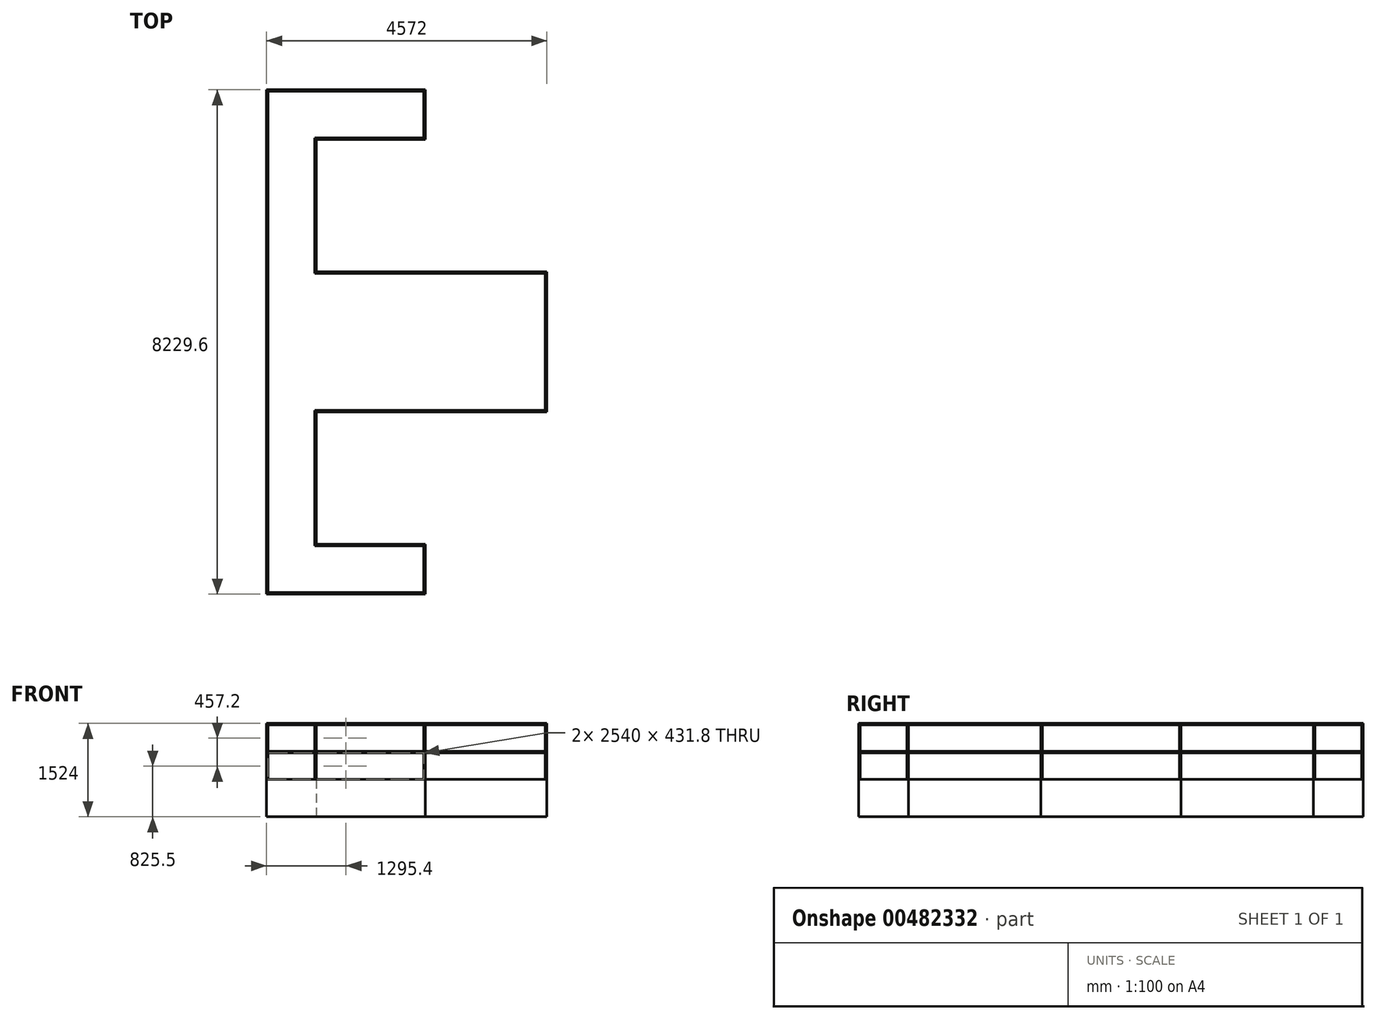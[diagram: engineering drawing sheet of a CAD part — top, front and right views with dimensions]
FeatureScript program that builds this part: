
annotation { "Feature Type Name" : "Feature", "Feature Type Description" : "" }
export const myFeature = defineFeature(function(context is Context, id is Id, definition is map)
    precondition{}
    {
        {
            var Q0;
            Q0=qCreatedBy(makeId("Top.planeOp"),FACE);
            var sketch = newSketch(context, id + "F0", { "sketchPlane" : qUnion([Q0])});
            skLineSegment(sketch, "E0", {"start": v(0, 0) * mm, "end": v(3759.2, 0) * mm});
            skLineSegment(sketch, "E1", {"start": v(3759.2, 0) * mm, "end": v(3759.2, 2286) * mm});
            skLineSegment(sketch, "E2", {"start": v(3759.2, 2286) * mm, "end": v(0, 2286) * mm});
            skLineSegment(sketch, "E3", {"start": v(0, 2286) * mm, "end": v(0, 4445) * mm});
            skLineSegment(sketch, "E4", {"start": v(0, 4445) * mm, "end": v(1778, 4445) * mm});
            skLineSegment(sketch, "E5", {"start": v(1778, 5257.8) * mm, "end": v(-812.8, 5257.8) * mm});
            skLineSegment(sketch, "E6", {"start": v(-812.8, 5257.8) * mm, "end": v(-812.8, -2971.8) * mm});
            skLineSegment(sketch, "E7", {"start": v(-812.8, -2971.8) * mm, "end": v(1778, -2971.8) * mm});
            skLineSegment(sketch, "E8", {"start": v(1778, -2971.8) * mm, "end": v(1778, -2159) * mm});
            skLineSegment(sketch, "E9", {"start": v(1778, -2159) * mm, "end": v(0, -2159) * mm});
            skLineSegment(sketch, "E10", {"start": v(0, -2159) * mm, "end": v(0, 0) * mm});
            skLineSegment(sketch, "E11", {"start": v(1778, 5257.8) * mm, "end": v(1778, 4445) * mm});
            skSolve(sketch);
        }
        {
            var Q0;
            Q0 = qSketchRegion(id + "F0", true);
            extrude(context, id + "F1", {"entities" : qUnion([Q0]), "depth" : 609.6 * mm, "offsetDistance" : 25.4 * mm});
        }
        {
            var Q0;
            Q0=makeQuery(id+"F1.opExtrude","CAP_FACE",FACE,{"disambiguationData":[OSD([sQuery(id+"F0.wireOp",EDGE,"E0"),sQuery(id+"F0.wireOp",EDGE,"E1"),sQuery(id+"F0.wireOp",EDGE,"E2"),sQuery(id+"F0.wireOp",EDGE,"E3"),sQuery(id+"F0.wireOp",EDGE,"E4"),sQuery(id+"F0.wireOp",EDGE,"E5"),sQuery(id+"F0.wireOp",EDGE,"E6"),sQuery(id+"F0.wireOp",EDGE,"E7"),sQuery(id+"F0.wireOp",EDGE,"E8"),sQuery(id+"F0.wireOp",EDGE,"E9"),sQuery(id+"F0.wireOp",EDGE,"E10"),sQuery(id+"F0.wireOp",EDGE,"E11")])],"isStart":false});
            var sketch = newSketch(context, id + "F2", { "sketchPlane" : qUnion([Q0])});
            skLineSegment(sketch, "E12.0", {"start": v(-787.4, -2946.4) * mm, "end": v(1752.6, -2946.4) * mm});
            skLineSegment(sketch, "E12.1", {"start": v(3733.8, 25.4) * mm, "end": v(3733.8, 2260.6) * mm});
            skLineSegment(sketch, "E12.2", {"start": v(-25.4, 25.4) * mm, "end": v(3733.8, 25.4) * mm});
            skLineSegment(sketch, "E12.3", {"start": v(-25.4, -2184.4) * mm, "end": v(-25.4, 25.4) * mm});
            skLineSegment(sketch, "E12.4", {"start": v(1752.6, -2184.4) * mm, "end": v(-25.4, -2184.4) * mm});
            skLineSegment(sketch, "E12.5", {"start": v(3733.8, 2260.6) * mm, "end": v(-25.4, 2260.6) * mm});
            skLineSegment(sketch, "E12.6", {"start": v(1752.6, -2946.4) * mm, "end": v(1752.6, -2184.4) * mm});
            skLineSegment(sketch, "E12.7", {"start": v(-25.4, 2260.6) * mm, "end": v(-25.4, 4470.4) * mm});
            skLineSegment(sketch, "E12.8", {"start": v(-25.4, 4470.4) * mm, "end": v(1752.6, 4470.4) * mm});
            skLineSegment(sketch, "E12.9", {"start": v(1752.6, 4470.4) * mm, "end": v(1752.6, 5232.4) * mm});
            skLineSegment(sketch, "E12.10", {"start": v(1752.6, 5232.4) * mm, "end": v(-787.4, 5232.4) * mm});
            skLineSegment(sketch, "E12.11", {"start": v(-787.4, 5232.4) * mm, "end": v(-787.4, -2946.4) * mm});
            skSolve(sketch);
        }
        {
            var Q0;
            Q0=makeQuery(id+"F2.imprint","IMPRINT",FACE,{"disambiguationData":[TD([[makeQuery(id+"F2.imprint","IMPRINT",EDGE,{"derivedFrom":sQuery(id+"F2.wireOp",EDGE,"E12.0")}),-1.0]])]});
            extrude(context, id + "F3", {"entities" : qUnion([Q0]), "operationType" : NewBodyOperationType.ADD, "depth" : 914.4 * mm, "offsetDistance" : 25.4 * mm});
        }
        {
            var Q0;
            {var subQ0=sQuery(id+"F0.wireOp",EDGE,"E6");Q0=makeQuery(id+"F3.boolean.opBoolean","MERGE",FACE,{"derivedFrom":[makeQuery(id+"F1.opExtrude","SWEPT_FACE",FACE,{"disambiguationData":[OSD([subQ0])]}),makeQuery(id+"F3.opExtrude","SWEPT_FACE",FACE,{"disambiguationData":[OSD([subQ0])]})]});}
            var sketch = newSketch(context, id + "F4", { "sketchPlane" : qUnion([Q0])});
            skLineSegment(sketch, "E13.bottom", {"start": v(-5232.4, 1498.6) * mm, "end": v(2946.4, 1498.6) * mm});
            skLineSegment(sketch, "E13.top", {"start": v(-5232.4, 1066.8) * mm, "end": v(2946.4, 1066.8) * mm});
            skLineSegment(sketch, "E13.left", {"start": v(-5232.4, 1498.6) * mm, "end": v(-5232.4, 1066.8) * mm});
            skLineSegment(sketch, "E13.right", {"start": v(2946.4, 1498.6) * mm, "end": v(2946.4, 1066.8) * mm});
            skLineSegment(sketch, "E14.bottom", {"start": v(-5232.4, 1041.4) * mm, "end": v(2946.4, 1041.4) * mm});
            skLineSegment(sketch, "E14.top", {"start": v(-5232.4, 609.6) * mm, "end": v(2946.4, 609.6) * mm});
            skLineSegment(sketch, "E14.left", {"start": v(-5232.4, 1041.4) * mm, "end": v(-5232.4, 609.6) * mm});
            skLineSegment(sketch, "E14.right", {"start": v(2946.4, 1041.4) * mm, "end": v(2946.4, 609.6) * mm});
            skSolve(sketch);
        }
        {
            var Q0;
            Q0 = qSketchRegion(id + "F4", true);
            extrude(context, id + "F5", {"entities" : qUnion([Q0]), "operationType" : NewBodyOperationType.REMOVE, "oppositeDirection" : true, "depth" : 50.8 * mm, "offsetDistance" : 25.4 * mm});
        }
        {
            var Q0;
            {var subQ0=sQuery(id+"F0.wireOp",EDGE,"E7");Q0=makeQuery(id+"F3.boolean.opBoolean","MERGE",FACE,{"derivedFrom":[makeQuery(id+"F1.opExtrude","SWEPT_FACE",FACE,{"disambiguationData":[OSD([subQ0])]}),makeQuery(id+"F3.opExtrude","SWEPT_FACE",FACE,{"disambiguationData":[OSD([subQ0])]})]});}
            var sketch = newSketch(context, id + "F6", { "sketchPlane" : qUnion([Q0])});
            skLineSegment(sketch, "E15.bottom", {"start": v(-787.4, 1498.6) * mm, "end": v(1752.6, 1498.6) * mm});
            skLineSegment(sketch, "E15.top", {"start": v(-787.4, 1066.8) * mm, "end": v(1752.6, 1066.8) * mm});
            skLineSegment(sketch, "E15.left", {"start": v(-787.4, 1498.6) * mm, "end": v(-787.4, 1066.8) * mm});
            skLineSegment(sketch, "E15.right", {"start": v(1752.6, 1498.6) * mm, "end": v(1752.6, 1066.8) * mm});
            skLineSegment(sketch, "E16.bottom", {"start": v(-787.4, 1041.4) * mm, "end": v(1752.6, 1041.4) * mm});
            skLineSegment(sketch, "E16.top", {"start": v(-787.4, 609.6) * mm, "end": v(1752.6, 609.6) * mm});
            skLineSegment(sketch, "E16.left", {"start": v(-787.4, 1041.4) * mm, "end": v(-787.4, 609.6) * mm});
            skLineSegment(sketch, "E16.right", {"start": v(1752.6, 1041.4) * mm, "end": v(1752.6, 609.6) * mm});
            skSolve(sketch);
        }
        {
            var Q0;
            Q0 = qSketchRegion(id + "F6", true);
            extrude(context, id + "F7", {"entities" : qUnion([Q0]), "operationType" : NewBodyOperationType.REMOVE, "oppositeDirection" : true, "depth" : 76.2 * mm, "offsetDistance" : 25.4 * mm});
        }
        {
            var Q0;
            {var subQ0=sQuery(id+"F0.wireOp",EDGE,"E2");Q0=makeQuery(id+"F3.boolean.opBoolean","MERGE",FACE,{"derivedFrom":[makeQuery(id+"F1.opExtrude","SWEPT_FACE",FACE,{"disambiguationData":[OSD([subQ0])]}),makeQuery(id+"F3.opExtrude","SWEPT_FACE",FACE,{"disambiguationData":[OSD([subQ0])]})]});}
            var sketch = newSketch(context, id + "F8", { "sketchPlane" : qUnion([Q0])});
            skLineSegment(sketch, "E17.bottom", {"start": v(-3733.8, 1498.6) * mm, "end": v(0, 1498.6) * mm});
            skLineSegment(sketch, "E17.top", {"start": v(-3733.8, 1066.8) * mm, "end": v(0, 1066.8) * mm});
            skLineSegment(sketch, "E17.right", {"start": v(0, 1498.6) * mm, "end": v(0, 1066.8) * mm});
            skLineSegment(sketch, "E18.bottom", {"start": v(0, 1041.4) * mm, "end": v(-3733.8, 1041.4) * mm});
            skLineSegment(sketch, "E18.top", {"start": v(0, 609.6) * mm, "end": v(-3784.6, 609.6) * mm});
            skLineSegment(sketch, "E18.left", {"start": v(0, 1041.4) * mm, "end": v(0, 609.6) * mm});
            skLineSegment(sketch, "E18.right", {"start": v(-3733.8, 1041.4) * mm, "end": v(-3733.8, 609.6) * mm});
            skLineSegment(sketch, "E19", {"start": v(-3733.8, 1498.6) * mm, "end": v(-3733.8, 1066.8) * mm});
            skSolve(sketch);
        }
        {
            var Q0;
            Q0 = qSketchRegion(id + "F8", true);
            extrude(context, id + "F9", {"entities" : qUnion([Q0]), "operationType" : NewBodyOperationType.REMOVE, "oppositeDirection" : true, "depth" : 76.2 * mm, "offsetDistance" : 25.4 * mm});
        }
        {
            var Q0;
            {var subQ0=sQuery(id+"F0.wireOp",EDGE,"VQ2aJ4W9-NI6z-mINO-OSkM-DMRvhCzpdo2V");var subQ1=sQuery(id+"F0.wireOp",EDGE,"E8");var subQ2=sQuery(id+"F0.wireOp",EDGE,"E1");Q0=makeQuery(id+"F3.boolean.opBoolean","MERGE",FACE,{"derivedFrom":[makeQuery(id+"F1.opExtrude","SWEPT_FACE",FACE,{"disambiguationData":[OSD([subQ2,subQ1,subQ0])]}),makeQuery(id+"F3.opExtrude","SWEPT_FACE",FACE,{"disambiguationData":[OSD([subQ2,subQ1,subQ0])]})]});}
            var sketch = newSketch(context, id + "F10", { "sketchPlane" : qUnion([Q0])});
            skLineSegment(sketch, "E20.bottom", {"start": v(25.4, 1498.6) * mm, "end": v(2260.6, 1498.6) * mm});
            skLineSegment(sketch, "E20.top", {"start": v(25.4, 1066.8) * mm, "end": v(2260.6, 1066.8) * mm});
            skLineSegment(sketch, "E20.left", {"start": v(25.4, 1498.6) * mm, "end": v(25.4, 1066.8) * mm});
            skLineSegment(sketch, "E20.right", {"start": v(2260.6, 1498.6) * mm, "end": v(2260.6, 1066.8) * mm});
            skLineSegment(sketch, "E21.bottom", {"start": v(2260.6, 1041.4) * mm, "end": v(25.4, 1041.4) * mm});
            skLineSegment(sketch, "E21.top", {"start": v(2260.6, 609.6) * mm, "end": v(25.4, 609.6) * mm});
            skLineSegment(sketch, "E21.left", {"start": v(2260.6, 1041.4) * mm, "end": v(2260.6, 609.6) * mm});
            skLineSegment(sketch, "E21.right", {"start": v(25.4, 1041.4) * mm, "end": v(25.4, 609.6) * mm});
            skSolve(sketch);
        }
        {
            var Q0;
            Q0 = qSketchRegion(id + "F10", true);
            extrude(context, id + "F11", {"entities" : qUnion([Q0]), "operationType" : NewBodyOperationType.REMOVE, "oppositeDirection" : true, "depth" : 76.2 * mm, "offsetDistance" : 25.4 * mm});
        }
        {
            var Q0;
            {var subQ0=sQuery(id+"F0.wireOp",EDGE,"E5");Q0=makeQuery(id+"F3.boolean.opBoolean","MERGE",FACE,{"derivedFrom":[makeQuery(id+"F1.opExtrude","SWEPT_FACE",FACE,{"disambiguationData":[OSD([subQ0])]}),makeQuery(id+"F3.opExtrude","SWEPT_FACE",FACE,{"disambiguationData":[OSD([subQ0])]})]});}
            var sketch = newSketch(context, id + "F12", { "sketchPlane" : qUnion([Q0])});
            skLineSegment(sketch, "E22.bottom", {"start": v(-1752.6, 1066.8) * mm, "end": v(787.4, 1066.8) * mm});
            skLineSegment(sketch, "E22.top", {"start": v(-1752.6, 1498.6) * mm, "end": v(787.4, 1498.6) * mm});
            skLineSegment(sketch, "E22.left", {"start": v(-1752.6, 1066.8) * mm, "end": v(-1752.6, 1498.6) * mm});
            skLineSegment(sketch, "E22.right", {"start": v(787.4, 1066.8) * mm, "end": v(787.4, 1498.6) * mm});
            skLineSegment(sketch, "E23.bottom", {"start": v(787.4, 1041.4) * mm, "end": v(-1752.6, 1041.4) * mm});
            skLineSegment(sketch, "E23.top", {"start": v(787.4, 609.6) * mm, "end": v(-1752.6, 609.6) * mm});
            skLineSegment(sketch, "E23.left", {"start": v(787.4, 1041.4) * mm, "end": v(787.4, 609.6) * mm});
            skLineSegment(sketch, "E23.right", {"start": v(-1752.6, 1041.4) * mm, "end": v(-1752.6, 609.6) * mm});
            skSolve(sketch);
        }
        {
            var Q0;
            Q0 = qSketchRegion(id + "F12", true);
            extrude(context, id + "F13", {"entities" : qUnion([Q0]), "operationType" : NewBodyOperationType.REMOVE, "oppositeDirection" : true, "depth" : 76.2 * mm, "offsetDistance" : 25.4 * mm});
        }
        {
            var Q0;
            {var subQ0=sQuery(id+"F0.wireOp",EDGE,"E11");Q0=makeQuery(id+"F3.boolean.opBoolean","MERGE",FACE,{"derivedFrom":[makeQuery(id+"F1.opExtrude","SWEPT_FACE",FACE,{"disambiguationData":[OSD([subQ0])]}),makeQuery(id+"F3.opExtrude","SWEPT_FACE",FACE,{"disambiguationData":[OSD([subQ0])]})]});}
            var sketch = newSketch(context, id + "F14", { "sketchPlane" : qUnion([Q0])});
            skLineSegment(sketch, "E24.bottom", {"start": v(4470.4, 1498.6) * mm, "end": v(5232.4, 1498.6) * mm});
            skLineSegment(sketch, "E24.top", {"start": v(4470.4, 1066.8) * mm, "end": v(5232.4, 1066.8) * mm});
            skLineSegment(sketch, "E24.left", {"start": v(4470.4, 1498.6) * mm, "end": v(4470.4, 1066.8) * mm});
            skLineSegment(sketch, "E24.right", {"start": v(5232.4, 1498.6) * mm, "end": v(5232.4, 1066.8) * mm});
            skLineSegment(sketch, "E25.bottom", {"start": v(5232.4, 1041.4) * mm, "end": v(4470.4, 1041.4) * mm});
            skLineSegment(sketch, "E25.top", {"start": v(5232.4, 609.6) * mm, "end": v(4470.4, 609.6) * mm});
            skLineSegment(sketch, "E25.left", {"start": v(5232.4, 1041.4) * mm, "end": v(5232.4, 609.6) * mm});
            skLineSegment(sketch, "E25.right", {"start": v(4470.4, 1041.4) * mm, "end": v(4470.4, 609.6) * mm});
            skSolve(sketch);
        }
        {
            var Q0;
            Q0 = qSketchRegion(id + "F14", true);
            extrude(context, id + "F15", {"entities" : qUnion([Q0]), "operationType" : NewBodyOperationType.REMOVE, "oppositeDirection" : true, "depth" : 76.2 * mm, "offsetDistance" : 25.4 * mm});
        }
        {
            var Q0;
            {var subQ0=sQuery(id+"F0.wireOp",EDGE,"E3");Q0=makeQuery(id+"F9.boolean.opBoolean","MERGE",FACE,{"derivedFrom":[makeQuery(id+"F3.boolean.opBoolean","MERGE",FACE,{"derivedFrom":[makeQuery(id+"F1.opExtrude","SWEPT_FACE",FACE,{"disambiguationData":[OSD([subQ0])]}),makeQuery(id+"F3.opExtrude","SWEPT_FACE",FACE,{"disambiguationData":[OSD([subQ0])]})]}),makeQuery(id+"F9.opExtrude","SWEPT_FACE",FACE,{"disambiguationData":[OSD([sQuery(id+"F8.wireOp",EDGE,"E17.right")])]}),makeQuery(id+"F9.opExtrude","SWEPT_FACE",FACE,{"disambiguationData":[OSD([sQuery(id+"F8.wireOp",EDGE,"E18.left")])]})]});}
            var sketch = newSketch(context, id + "F16", { "sketchPlane" : qUnion([Q0])});
            skLineSegment(sketch, "E26.bottom", {"start": v(2286, 1498.6) * mm, "end": v(4445, 1498.6) * mm});
            skLineSegment(sketch, "E26.top", {"start": v(2286, 1066.8) * mm, "end": v(4445, 1066.8) * mm});
            skLineSegment(sketch, "E26.left", {"start": v(2286, 1498.6) * mm, "end": v(2286, 1066.8) * mm});
            skLineSegment(sketch, "E26.right", {"start": v(4445, 1498.6) * mm, "end": v(4445, 1066.8) * mm});
            skLineSegment(sketch, "E27.bottom", {"start": v(2286, 1041.4) * mm, "end": v(4445, 1041.4) * mm});
            skLineSegment(sketch, "E27.top", {"start": v(2286, 609.6) * mm, "end": v(4445, 609.6) * mm});
            skLineSegment(sketch, "E27.left", {"start": v(2286, 1041.4) * mm, "end": v(2286, 609.6) * mm});
            skLineSegment(sketch, "E27.right", {"start": v(4445, 1041.4) * mm, "end": v(4445, 609.6) * mm});
            skSolve(sketch);
        }
        {
            var Q0;
            Q0 = qSketchRegion(id + "F16", true);
            extrude(context, id + "F17", {"entities" : qUnion([Q0]), "operationType" : NewBodyOperationType.REMOVE, "oppositeDirection" : true, "depth" : 76.2 * mm, "offsetDistance" : 25.4 * mm});
        }
        {
            var Q0;
            {var subQ0=sQuery(id+"F0.wireOp",EDGE,"E4");Q0=makeQuery(id+"F17.boolean.opBoolean","MERGE",FACE,{"derivedFrom":[makeQuery(id+"F3.boolean.opBoolean","MERGE",FACE,{"derivedFrom":[makeQuery(id+"F1.opExtrude","SWEPT_FACE",FACE,{"disambiguationData":[OSD([subQ0])]}),makeQuery(id+"F3.opExtrude","SWEPT_FACE",FACE,{"disambiguationData":[OSD([subQ0])]})]}),makeQuery(id+"F17.opExtrude","SWEPT_FACE",FACE,{"disambiguationData":[OSD([sQuery(id+"F16.wireOp",EDGE,"E26.right")])]}),makeQuery(id+"F17.opExtrude","SWEPT_FACE",FACE,{"disambiguationData":[OSD([sQuery(id+"F16.wireOp",EDGE,"E27.right")])]})]});}
            var sketch = newSketch(context, id + "F18", { "sketchPlane" : qUnion([Q0])});
            skLineSegment(sketch, "E28.bottom", {"start": v(0, 1498.6) * mm, "end": v(1752.6, 1498.6) * mm});
            skLineSegment(sketch, "E28.top", {"start": v(0, 1066.8) * mm, "end": v(1752.6, 1066.8) * mm});
            skLineSegment(sketch, "E28.left", {"start": v(0, 1498.6) * mm, "end": v(0, 1066.8) * mm});
            skLineSegment(sketch, "E28.right", {"start": v(1752.6, 1498.6) * mm, "end": v(1752.6, 1066.8) * mm});
            skLineSegment(sketch, "E29.bottom", {"start": v(1752.6, 1041.4) * mm, "end": v(0, 1041.4) * mm});
            skLineSegment(sketch, "E29.top", {"start": v(1752.6, 609.6) * mm, "end": v(0, 609.6) * mm});
            skLineSegment(sketch, "E29.left", {"start": v(1752.6, 1041.4) * mm, "end": v(1752.6, 609.6) * mm});
            skLineSegment(sketch, "E29.right", {"start": v(0, 1041.4) * mm, "end": v(0, 609.6) * mm});
            skSolve(sketch);
        }
        {
            var Q0;
            Q0 = qSketchRegion(id + "F18", true);
            extrude(context, id + "F19", {"entities" : qUnion([Q0]), "operationType" : NewBodyOperationType.REMOVE, "oppositeDirection" : true, "depth" : 76.2 * mm, "offsetDistance" : 25.4 * mm});
        }
        {
            var Q0;
            {var subQ0=sQuery(id+"F0.wireOp",EDGE,"E9");Q0=makeQuery(id+"F3.boolean.opBoolean","MERGE",FACE,{"derivedFrom":[makeQuery(id+"F1.opExtrude","SWEPT_FACE",FACE,{"disambiguationData":[OSD([subQ0])]}),makeQuery(id+"F3.opExtrude","SWEPT_FACE",FACE,{"disambiguationData":[OSD([subQ0])]})]});}
            var sketch = newSketch(context, id + "F20", { "sketchPlane" : qUnion([Q0])});
            skLineSegment(sketch, "E30.bottom", {"start": v(-1752.6, 1498.6) * mm, "end": v(0, 1498.6) * mm});
            skLineSegment(sketch, "E30.top", {"start": v(-1752.6, 1066.8) * mm, "end": v(0, 1066.8) * mm});
            skLineSegment(sketch, "E30.left", {"start": v(-1752.6, 1498.6) * mm, "end": v(-1752.6, 1066.8) * mm});
            skLineSegment(sketch, "E30.right", {"start": v(0, 1498.6) * mm, "end": v(0, 1066.8) * mm});
            skLineSegment(sketch, "E31.bottom", {"start": v(0, 1041.4) * mm, "end": v(-1752.6, 1041.4) * mm});
            skLineSegment(sketch, "E31.top", {"start": v(0, 609.6) * mm, "end": v(-1752.6, 609.6) * mm});
            skLineSegment(sketch, "E31.left", {"start": v(0, 1041.4) * mm, "end": v(0, 609.6) * mm});
            skLineSegment(sketch, "E31.right", {"start": v(-1752.6, 1041.4) * mm, "end": v(-1752.6, 609.6) * mm});
            skSolve(sketch);
        }
        {
            var Q0;
            Q0 = qSketchRegion(id + "F20", true);
            extrude(context, id + "F21", {"entities" : qUnion([Q0]), "operationType" : NewBodyOperationType.REMOVE, "oppositeDirection" : true, "depth" : 50.8 * mm, "offsetDistance" : 25.4 * mm});
        }
        {
            var Q0;
            {var subQ0=sQuery(id+"F0.wireOp",EDGE,"E8");Q0=makeQuery(id+"F3.boolean.opBoolean","MERGE",FACE,{"derivedFrom":[makeQuery(id+"F1.opExtrude","SWEPT_FACE",FACE,{"disambiguationData":[OSD([subQ0])]}),makeQuery(id+"F3.opExtrude","SWEPT_FACE",FACE,{"disambiguationData":[OSD([subQ0])]})]});}
            var sketch = newSketch(context, id + "F22", { "sketchPlane" : qUnion([Q0])});
            skLineSegment(sketch, "E32.bottom", {"start": v(-2946.4, 1498.6) * mm, "end": v(-2184.4, 1498.6) * mm});
            skLineSegment(sketch, "E32.top", {"start": v(-2946.4, 1066.8) * mm, "end": v(-2184.4, 1066.8) * mm});
            skLineSegment(sketch, "E32.left", {"start": v(-2946.4, 1498.6) * mm, "end": v(-2946.4, 1066.8) * mm});
            skLineSegment(sketch, "E32.right", {"start": v(-2184.4, 1498.6) * mm, "end": v(-2184.4, 1066.8) * mm});
            skLineSegment(sketch, "E33.bottom", {"start": v(-2946.4, 1041.4) * mm, "end": v(-2184.4, 1041.4) * mm});
            skLineSegment(sketch, "E33.top", {"start": v(-2946.4, 609.6) * mm, "end": v(-2184.4, 609.6) * mm});
            skLineSegment(sketch, "E33.left", {"start": v(-2946.4, 1041.4) * mm, "end": v(-2946.4, 609.6) * mm});
            skLineSegment(sketch, "E33.right", {"start": v(-2184.4, 1041.4) * mm, "end": v(-2184.4, 609.6) * mm});
            skSolve(sketch);
        }
        {
            var Q0;
            Q0 = qSketchRegion(id + "F22", true);
            extrude(context, id + "F23", {"entities" : qUnion([Q0]), "operationType" : NewBodyOperationType.REMOVE, "oppositeDirection" : true, "depth" : 25.4 * mm, "offsetDistance" : 25.4 * mm});
        }
        {
            var Q0;
            {var subQ0=sQuery(id+"F0.wireOp",EDGE,"E10");Q0=makeQuery(id+"F21.boolean.opBoolean","MERGE",FACE,{"derivedFrom":[makeQuery(id+"F3.boolean.opBoolean","MERGE",FACE,{"derivedFrom":[makeQuery(id+"F1.opExtrude","SWEPT_FACE",FACE,{"disambiguationData":[OSD([subQ0])]}),makeQuery(id+"F3.opExtrude","SWEPT_FACE",FACE,{"disambiguationData":[OSD([subQ0])]})]}),makeQuery(id+"F21.opExtrude","SWEPT_FACE",FACE,{"disambiguationData":[OSD([sQuery(id+"F20.wireOp",EDGE,"E30.right")])]}),makeQuery(id+"F21.opExtrude","SWEPT_FACE",FACE,{"disambiguationData":[OSD([sQuery(id+"F20.wireOp",EDGE,"E31.left")])]})]});}
            var sketch = newSketch(context, id + "F24", { "sketchPlane" : qUnion([Q0])});
            skLineSegment(sketch, "E34.bottom", {"start": v(-2159, 1498.6) * mm, "end": v(0, 1498.6) * mm});
            skLineSegment(sketch, "E34.top", {"start": v(-2159, 1066.8) * mm, "end": v(0, 1066.8) * mm});
            skLineSegment(sketch, "E34.left", {"start": v(-2159, 1498.6) * mm, "end": v(-2159, 1066.8) * mm});
            skLineSegment(sketch, "E34.right", {"start": v(0, 1498.6) * mm, "end": v(0, 1066.8) * mm});
            skLineSegment(sketch, "E35.bottom", {"start": v(0, 1041.4) * mm, "end": v(-2159, 1041.4) * mm});
            skLineSegment(sketch, "E35.top", {"start": v(0, 609.6) * mm, "end": v(-2159, 609.6) * mm});
            skLineSegment(sketch, "E35.left", {"start": v(0, 1041.4) * mm, "end": v(0, 609.6) * mm});
            skLineSegment(sketch, "E35.right", {"start": v(-2159, 1041.4) * mm, "end": v(-2159, 609.6) * mm});
            skSolve(sketch);
        }
        {
            var Q0;
            Q0 = qSketchRegion(id + "F24", true);
            extrude(context, id + "F25", {"entities" : qUnion([Q0]), "operationType" : NewBodyOperationType.REMOVE, "oppositeDirection" : true, "depth" : 25.4 * mm, "offsetDistance" : 25.4 * mm});
        }
        {
            var Q0;
            {var subQ0=sQuery(id+"F0.wireOp",EDGE,"E0");Q0=makeQuery(id+"F25.boolean.opBoolean","MERGE",FACE,{"derivedFrom":[makeQuery(id+"F3.boolean.opBoolean","MERGE",FACE,{"derivedFrom":[makeQuery(id+"F1.opExtrude","SWEPT_FACE",FACE,{"disambiguationData":[OSD([subQ0])]}),makeQuery(id+"F3.opExtrude","SWEPT_FACE",FACE,{"disambiguationData":[OSD([subQ0])]})]}),makeQuery(id+"F25.opExtrude","SWEPT_FACE",FACE,{"disambiguationData":[OSD([sQuery(id+"F24.wireOp",EDGE,"E34.right")])]}),makeQuery(id+"F25.opExtrude","SWEPT_FACE",FACE,{"disambiguationData":[OSD([sQuery(id+"F24.wireOp",EDGE,"E35.left")])]})]});}
            var sketch = newSketch(context, id + "F26", { "sketchPlane" : qUnion([Q0])});
            skLineSegment(sketch, "E36.bottom", {"start": v(0, 1498.6) * mm, "end": v(3733.8, 1498.6) * mm});
            skLineSegment(sketch, "E36.top", {"start": v(0, 1066.8) * mm, "end": v(3733.8, 1066.8) * mm});
            skLineSegment(sketch, "E36.left", {"start": v(0, 1498.6) * mm, "end": v(0, 1066.8) * mm});
            skLineSegment(sketch, "E36.right", {"start": v(3733.8, 1498.6) * mm, "end": v(3733.8, 1066.8) * mm});
            skLineSegment(sketch, "E37.bottom", {"start": v(3733.8, 1041.4) * mm, "end": v(0, 1041.4) * mm});
            skLineSegment(sketch, "E37.top", {"start": v(3733.8, 609.6) * mm, "end": v(0, 609.6) * mm});
            skLineSegment(sketch, "E37.left", {"start": v(3733.8, 1041.4) * mm, "end": v(3733.8, 609.6) * mm});
            skLineSegment(sketch, "E37.right", {"start": v(0, 1041.4) * mm, "end": v(0, 609.6) * mm});
            skSolve(sketch);
        }
        {
            var Q0;
            Q0 = qSketchRegion(id + "F26", true);
            extrude(context, id + "F27", {"entities" : qUnion([Q0]), "operationType" : NewBodyOperationType.REMOVE, "oppositeDirection" : true, "depth" : 25.4 * mm, "offsetDistance" : 25.4 * mm});
        }
    });
